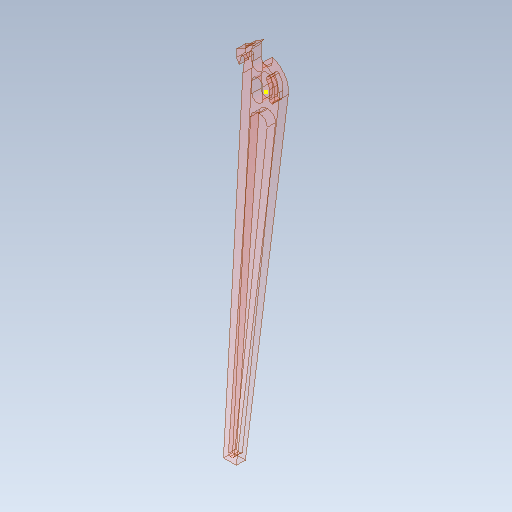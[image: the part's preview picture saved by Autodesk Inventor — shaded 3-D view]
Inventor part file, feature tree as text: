
AUTODESK INVENTOR PART (.ipt)
format: ipt  version: 2020.2 (Build 242310000, 310)  size: 645,120 bytes
history: native  units: mm
features: sketch x22, extrude x17, fillet x11, other x9, projected_geometry x8
ambient origin geometry x8: Origin, YZ Plane, XZ Plane, XY Plane, X Axis, Y Axis, Z Axis, Center Point
bodies: Body1 (feature_tree)
feature tree (67):
  other  "ソリッド1"
  sketch  "スケッチ1"
  extrude  "押し出し1"  Depth=6.0mm
  extrude  "押し出し2"  Depth=6.0mm
  sketch  "スケッチ4"
  fillet  "フィレット1"  Radius=3.0mm
  fillet  "フィレット2"  Radius=3.0mm
  fillet  "フィレット3"  Radius=6.0mm
  fillet  "フィレット4"  Radius=6.0mm
  extrude  "押し出し3"  Depth=6.0mm
  fillet  "フィレット5"  Radius=3.0mm
  sketch  "スケッチ6"
  extrude  "押し出し4"  Depth=7.0mm
  sketch  "スケッチ8"
  extrude  "押し出し5"  Depth=160.0mm
  extrude  "押し出し6"  Depth=15.0mm
  extrude  "押し出し7"  Depth=3.0mm
  fillet  "フィレット6"  Radius=5.0mm
  fillet  "フィレット7"  Radius=5.0mm
  extrude  "押し出し8"  Depth=5.0mm
  fillet  "フィレット8"  Radius=4.0mm
  sketch  "スケッチ11"
  sketch  "スケッチ12"
  extrude  "押し出し9"  Depth=4.0mm TaperAngle=0.0deg
  sketch  "スケッチ14"
  extrude  "押し出し10"  Depth=3.0mm
  extrude  "押し出し11"  Depth=4.0mm
  sketch  "スケッチ15"
  extrude  "押し出し12"  Depth=2.0mm
  sketch  "スケッチ17"
  extrude  "押し出し13"  Depth=1.0mm
  extrude  "押し出し14"  Depth=3.0mm
  sketch  "スケッチ20"
  sketch  "スケッチ21"
  extrude  "押し出し15"  Depth=8.0mm
  extrude  "押し出し16"  Depth=1.0mm
  fillet  "フィレット9"  Radius=5.0mm
  fillet  "フィレット10"  Radius=4.0mm
  extrude  "押し出し17"  Depth=3.0mm
  fillet  "フィレット11"  Radius=4.5mm
  sketch  "スケッチ2"
  sketch  "スケッチ3"
  sketch  "スケッチ5"
  sketch  "スケッチ7"
  sketch  "スケッチ9"
  sketch  "スケッチ10"
  projected_geometry  "投影ループ1"
  projected_geometry  "投影ループ2"
  sketch  "スケッチ13"
  projected_geometry  "投影ループ3"
  sketch  "スケッチ16"
  sketch  "スケッチ18"
  projected_geometry  "投影ループ4"
  sketch  "スケッチ19"
  projected_geometry  "投影ループ5"
  projected_geometry  "投影ループ6"
  projected_geometry  "投影ループ7"
  sketch  "スケッチ22"
  projected_geometry  "投影ループ8"
  other  "断面エッジを投影1"
  other  "断面エッジを投影2"
  other  "断面エッジを投影3"
  other  "断面エッジを投影4"
  other  "断面エッジを投影5"
  other  "断面エッジを投影6"
  other  "断面エッジを投影7"
  other  "断面エッジを投影8"
